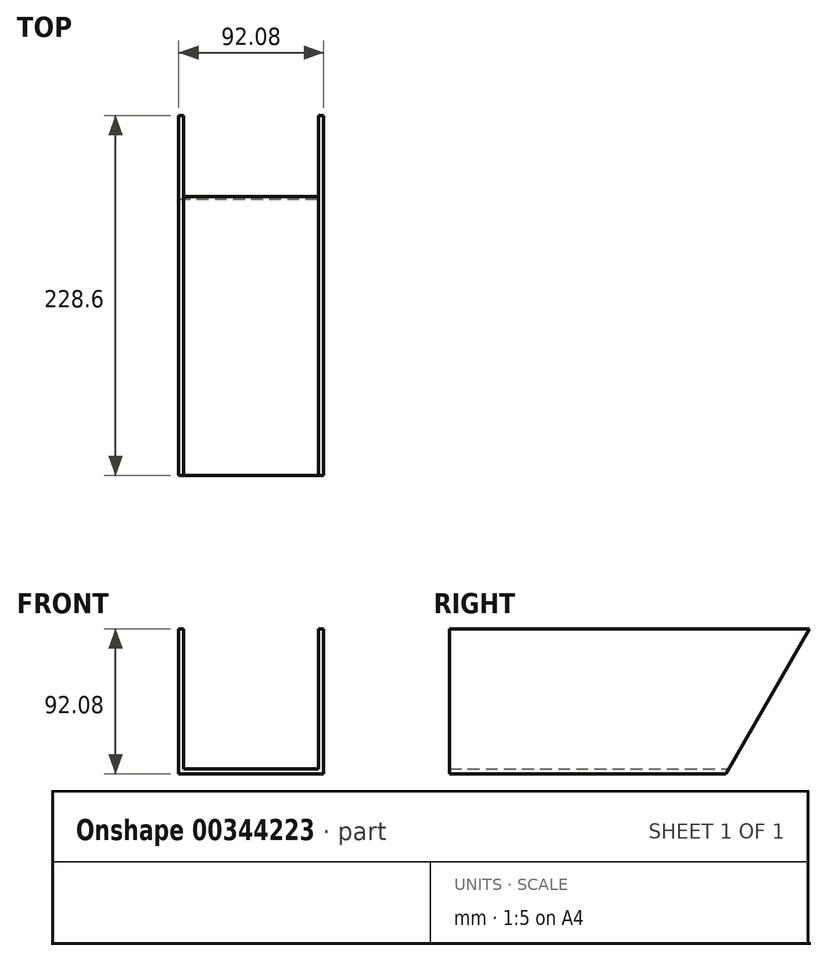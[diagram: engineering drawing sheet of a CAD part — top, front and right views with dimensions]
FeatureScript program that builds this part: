
annotation { "Feature Type Name" : "Feature", "Feature Type Description" : "" }
export const myFeature = defineFeature(function(context is Context, id is Id, definition is map)
    precondition{}
    {
        {
            var Q0;
            Q0=qCreatedBy(makeId("Front.planeOp"),FACE);
            var sketch = newSketch(context, id + "F0", { "sketchPlane" : qUnion([Q0])});
            skLineSegment(sketch, "E0", {"start": v(-51.54, 0) * mm, "end": v(40.54, 0) * mm});
            skLineSegment(sketch, "E1", {"start": v(40.54, 0) * mm, "end": v(40.54, 92.08) * mm});
            skLineSegment(sketch, "E2", {"start": v(40.54, 92.08) * mm, "end": v(37.36, 92.08) * mm});
            skLineSegment(sketch, "E3", {"start": v(37.36, 92.08) * mm, "end": v(37.36, 3.18) * mm});
            skLineSegment(sketch, "E4", {"start": v(37.36, 3.18) * mm, "end": v(-48.36, 3.17) * mm});
            skLineSegment(sketch, "E5", {"start": v(-48.36, 3.17) * mm, "end": v(-48.36, 92.08) * mm});
            skLineSegment(sketch, "E6", {"start": v(-48.36, 92.08) * mm, "end": v(-51.54, 92.08) * mm});
            skLineSegment(sketch, "E7", {"start": v(-51.54, 92.07) * mm, "end": v(-51.54, 0) * mm});
            skSolve(sketch);
        }
        {
            var Q0;
            Q0=makeQuery(id+"F0.imprint","IMPRINT",FACE,{"disambiguationData":[TD([[makeQuery(id+"F0.imprint","IMPRINT",EDGE,{"derivedFrom":sQuery(id+"F0.wireOp",EDGE,"E0")}),1.0]])]});
            extrude(context, id + "F1", {"entities" : qUnion([Q0]), "depth" : 228.6 * mm});
        }
        {
            var Q0;
            Q0=makeQuery(id+"F1.opExtrude","SWEPT_FACE",FACE,{"disambiguationData":[OSD([sQuery(id+"F0.wireOp",EDGE,"E1")])]});
            var sketch = newSketch(context, id + "F2", { "sketchPlane" : qUnion([Q0])});
            skLineSegment(sketch, "E8.0", {"start": v(0, 0) * mm, "end": v(0, 92.08) * mm});
            skLineSegment(sketch, "E9", {"start": v(0, 92.08) * mm, "end": v(-53.16, 0) * mm});
            skLineSegment(sketch, "E10", {"start": v(-53.16, 0) * mm, "end": v(0, 0) * mm});
            skSolve(sketch);
        }
        {
            var Q0;
            Q0=makeQuery(id+"F2.imprint","IMPRINT",FACE,{"disambiguationData":[TD([[makeQuery(id+"F2.imprint","IMPRINT",EDGE,{"derivedFrom":sQuery(id+"F2.wireOp",EDGE,"E8.0")}),1.0]])]});
            extrude(context, id + "F3", {"entities" : qUnion([Q0]), "operationType" : NewBodyOperationType.REMOVE, "endBound" : BoundingType.THROUGH_ALL, "oppositeDirection" : true, "depth" : 25.4 * mm});
        }
    });
